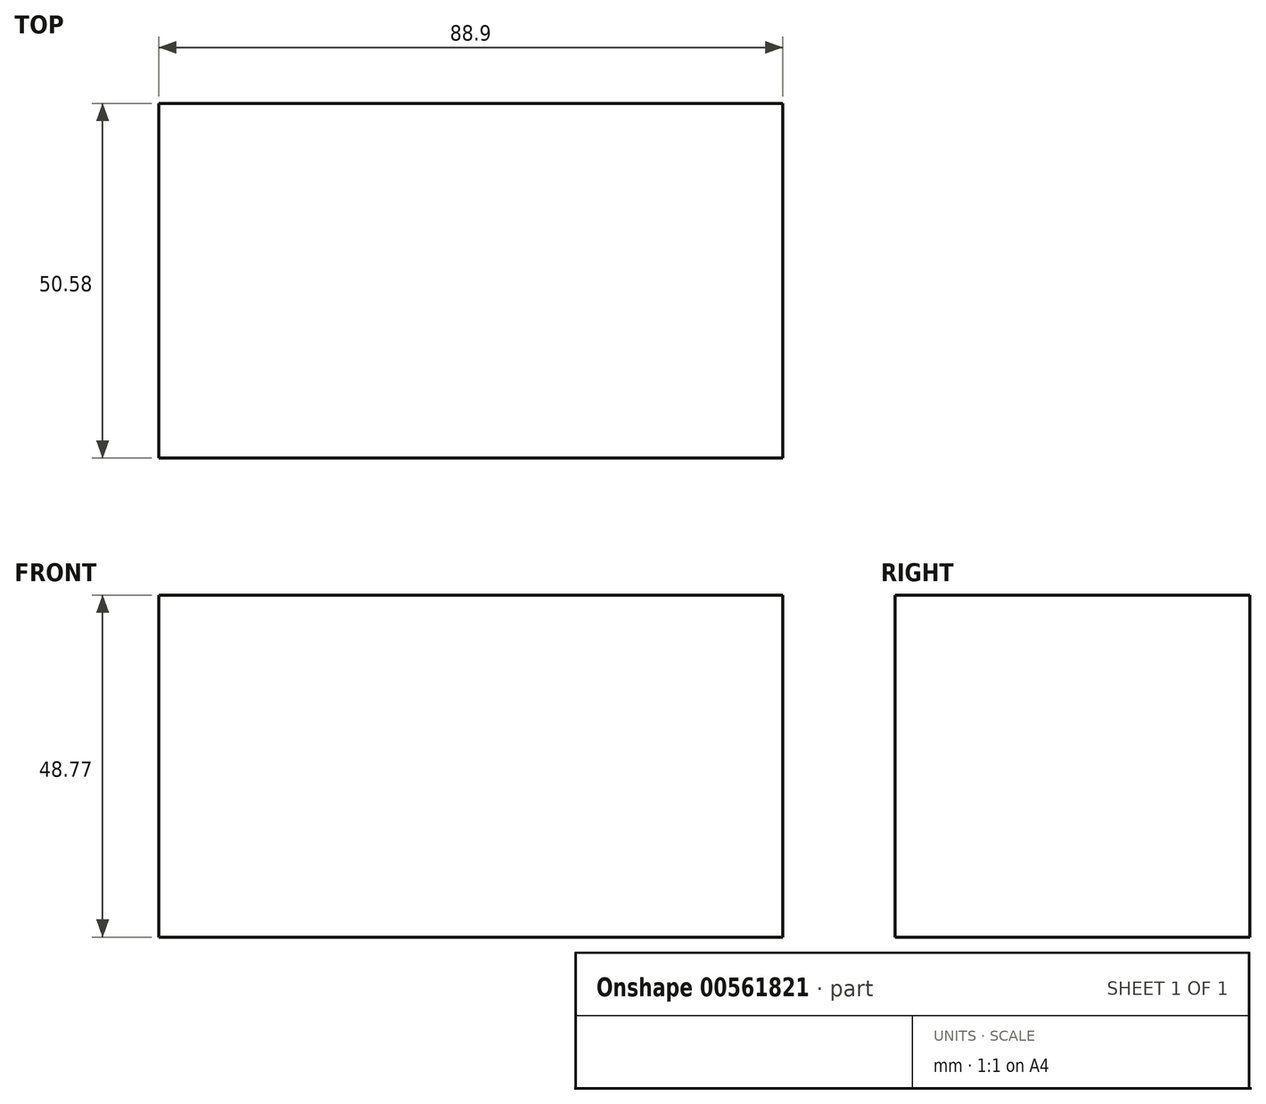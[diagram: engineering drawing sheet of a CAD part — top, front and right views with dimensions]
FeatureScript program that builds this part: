
annotation { "Feature Type Name" : "Feature", "Feature Type Description" : "" }
export const myFeature = defineFeature(function(context is Context, id is Id, definition is map)
    precondition{}
    {
        {
            var Q0;
            Q0=qCreatedBy(makeId("Front.planeOp"),FACE);
            var sketch = newSketch(context, id + "F0", { "sketchPlane" : qUnion([Q0])});
            skLineSegment(sketch, "E0.bottom", {"start": v(-44.45, 0) * mm, "end": v(44.45, 0) * mm});
            skLineSegment(sketch, "E0.top", {"start": v(-44.45, 48.77) * mm, "end": v(44.45, 48.77) * mm});
            skLineSegment(sketch, "E0.left", {"start": v(-44.45, 0) * mm, "end": v(-44.45, 48.77) * mm});
            skLineSegment(sketch, "E0.right", {"start": v(44.45, 0) * mm, "end": v(44.45, 48.77) * mm});
            skSolve(sketch);
        }
        {
            var Q0;
            Q0 = qSketchRegion(id + "F0", true);
            extrude(context, id + "F1", {"entities" : qUnion([Q0]), "endBound" : BoundingType.SYMMETRIC, "depth" : 50.57 * mm, "offsetDistance" : 25.4 * mm});
        }
    });
